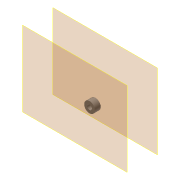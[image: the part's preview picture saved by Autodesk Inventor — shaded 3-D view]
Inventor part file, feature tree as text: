
AUTODESK INVENTOR PART (.ipt)
format: ipt  version: 2019.4 (Build 234330000, 330)  size: 81,408 bytes
history: native  units: mm
features: other x4, plane x2, extrude x1, sketch x1, reference x1
ambient origin geometry x8: Origin, YZ Plane, XZ Plane, XY Plane, X Axis, Y Axis, Z Axis, Center Point
bodies: Solid1 (feature_tree)
feature tree (9):
  plane  "Work Plane1"
  plane  "Work Plane2"
  extrude  "Extrusion1"  Depth=7.0mm TaperAngle=0.0deg
  sketch  "Sketch1"  dims[d0=3.0mm d1=7.0mm d2=0.0mm]
  reference  "Reference1"
  other  "Assembly_neje_slide_y_wellplateholder_20mmrod.iam"
  other  "Assembly_neje_slide_y_20mmrod:1"
  other  "Neje_slide_y_20mmrod_lowerplate:1"
  other  "Neje_slide_y_20mmrod_upperplate:1"
